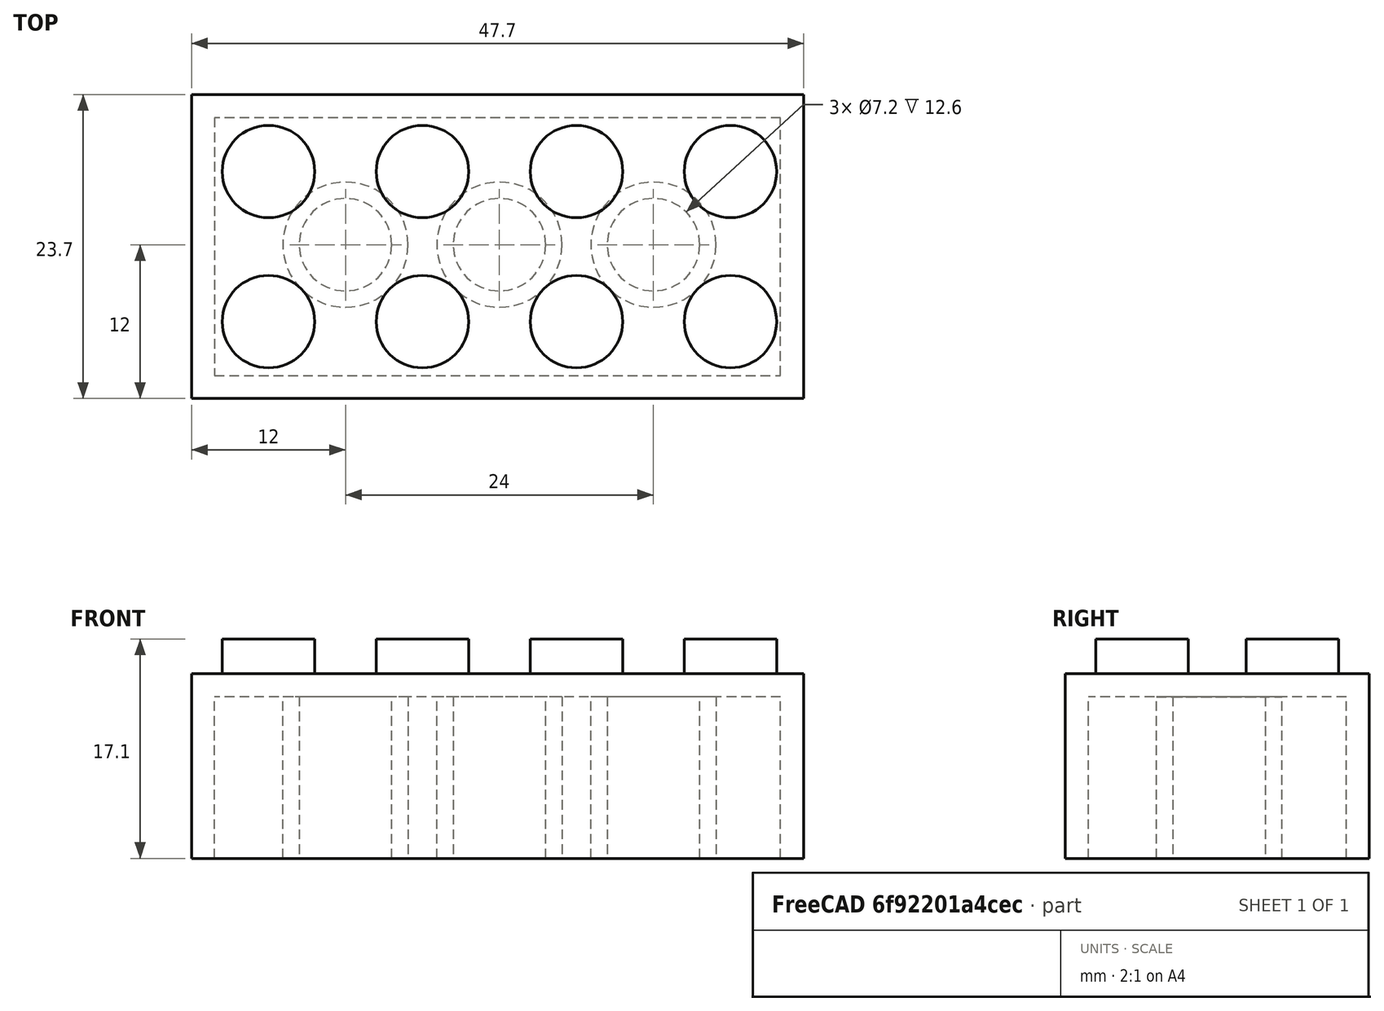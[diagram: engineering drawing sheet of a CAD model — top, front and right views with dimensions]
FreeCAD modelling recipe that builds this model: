
FCSTD DOCUMENT  (FreeCAD 0.19R17175 (Git))
Label: fem_lego
License: All rights reserved
LicenseURL: http://en.wikipedia.org/wiki/All_rights_reserved
objects: Sketcher::SketchObject×5, PartDesign::Pad×3, PartDesign::LinearPattern×3, PartDesign::Pocket×2, PartDesign::Body×1, Fem::FemMeshShapeNetgenObject×1, Fem::ConstraintFixed×1, Fem::ConstraintForce×1, App::MaterialObjectPython×1, Fem::FemSolverObjectPython×1, Fem::FemMeshObjectPython×1, Fem::FemResultObjectPython×1, Fem::FemAnalysis×1
note: 19 computed .brp shape members not serialized (recipe doc carries the construction recipe); baked Part::Feature solids carry a one-line shape summary decoded from their .brp

FEATURE [Sketcher::SketchObject] Sketch
  MapMode = 5
  Support = -> [XY_Plane]
  sketch-geometry (4):
    g0: LineSegment StartX=0 StartY=0 StartZ=0 EndX=47.7 EndY=0 EndZ=0
    g1: LineSegment StartX=47.7 StartY=0 StartZ=0 EndX=47.7 EndY=-23.7 EndZ=0
    g2: LineSegment StartX=47.7 StartY=-23.7 StartZ=0 EndX=0 EndY=-23.7 EndZ=0
    g3: LineSegment StartX=0 StartY=-23.7 StartZ=0 EndX=0 EndY=0 EndZ=0
  constraints (11):
    c: Coincident(g0,g1)
    c: Coincident(g1,g2)
    c: Coincident(g2,g3)
    c: Coincident(g3,g0)
    c: Horizontal(g0)
    c: Horizontal(g2)
    c: Vertical(g1)
    c: Vertical(g3)
    c: DistanceY(g3,g3) = 23.7
    c: DistanceX(g0,g0) = 47.7
    c: Coincident(g0,g-1)
FEATURE [PartDesign::Pad] Pad
  Length = 14.4
  Length2 = 100
  Profile = -> Sketch
  Type = 0
FEATURE [Sketcher::SketchObject] Sketch001
  ExternalGeometry = -> [Pad]
  MapMode = 5
  Placement = pos=(0,0,0) rot=(1,0,0;3.14159rad)
  Support = -> [Pad]
  sketch-geometry (4):
    g0: LineSegment StartX=1.8 StartY=21.9 StartZ=0 EndX=45.9 EndY=21.9 EndZ=0
    g1: LineSegment StartX=45.9 StartY=21.9 StartZ=0 EndX=45.9 EndY=1.8 EndZ=0
    g2: LineSegment StartX=45.9 StartY=1.8 StartZ=0 EndX=1.8 EndY=1.8 EndZ=0
    g3: LineSegment StartX=1.8 StartY=1.8 StartZ=0 EndX=1.8 EndY=21.9 EndZ=0
  constraints (12):
    c: Coincident(g0,g1)
    c: Coincident(g1,g2)
    c: Coincident(g2,g3)
    c: Coincident(g3,g0)
    c: Horizontal(g0)
    c: Horizontal(g2)
    c: Vertical(g1)
    c: Vertical(g3)
    c: DistanceX(g-4,g0) = 1.8
    c: DistanceY(g0,g-4) = 1.8
    c: DistanceX(g1,g-3) = 1.8
    c: DistanceY(g-3,g1) = 1.8
FEATURE [PartDesign::Pocket] Pocket
  BaseFeature = -> Pad
  Length = 12.6
  Length2 = 100
  Profile = -> Sketch001
  Type = 0
FEATURE [Sketcher::SketchObject] Sketch002
  ExternalGeometry = -> [Pocket]
  MapMode = 5
  Placement = pos=(0,0,14.4) rot=(0,0,1;0rad)
  Support = -> [Pocket]
  sketch-geometry (2):
    g0: Circle CenterX=6 CenterY=-6 CenterZ=0 NormalX=0 NormalY=0 NormalZ=1 AngleXU=0 Radius=3.6
    g1: Circle CenterX=6 CenterY=-17.7 CenterZ=0 NormalX=0 NormalY=0 NormalZ=1 AngleXU=0 Radius=3.6
  constraints (6):
    c: Radius(g0) = 3.6
    c: Radius(g1) = 3.6
    c: DistanceX(g-1,g0) = 6
    c: DistanceY(g0,g-1) = 6
    c: DistanceX(g-3,g1) = 6
    c: DistanceY(g-3,g1) = 6
FEATURE [PartDesign::Pad] Pad001
  BaseFeature = -> Pocket
  Length = 2.7
  Length2 = 100
  Profile = -> Sketch002
  Type = 0
FEATURE [PartDesign::LinearPattern] LinearPattern
  BaseFeature = -> Pad001
  Direction = -> Sketch002 [H_Axis]
  Length = 36
  Occurrences = 4
  Originals = -> [Pad001]
FEATURE [Sketcher::SketchObject] Sketch003
  ExternalGeometry = -> [LinearPattern]
  MapMode = 5
  Placement = pos=(0,0,12.6) rot=(1,0,0;3.14159rad)
  Support = -> [LinearPattern]
  sketch-geometry (1):
    g0: Circle CenterX=12 CenterY=11.7 CenterZ=0 NormalX=0 NormalY=0 NormalZ=1 AngleXU=0 Radius=4.8825
  constraints (3):
    c: Radius(g0) = 4.8825
    c: DistanceX(g-3,g0) = 10.2
    c: DistanceY(g0,g-3) = 10.2
FEATURE [PartDesign::Pad] Pad002
  BaseFeature = -> LinearPattern
  Length = 12.6
  Length2 = 100
  Profile = -> Sketch003
  Type = 0
FEATURE [PartDesign::LinearPattern] LinearPattern001
  BaseFeature = -> Pad002
  Direction = -> Sketch003 [H_Axis]
  Length = 24
  Occurrences = 3
  Originals = -> [Pad002]
FEATURE [Sketcher::SketchObject] Sketch004
  ExternalGeometry = -> [LinearPattern001]
  MapMode = 5
  Placement = pos=(0,0,1.8e-15) rot=(1,0,0;3.14159rad)
  Support = -> [LinearPattern001]
  sketch-geometry (1):
    g0: Circle CenterX=12 CenterY=11.7 CenterZ=0 NormalX=0 NormalY=0 NormalZ=1 AngleXU=0 Radius=3.6
  constraints (2):
    c: Coincident(g0,g-3)
    c: Radius(g0) = 3.6
FEATURE [PartDesign::Pocket] Pocket001
  BaseFeature = -> LinearPattern001
  Length = 12.6
  Length2 = 100
  Profile = -> Sketch004
  Type = 0
FEATURE [PartDesign::LinearPattern] LinearPattern002
  BaseFeature = -> Pocket001
  Direction = -> Sketch004 [H_Axis]
  Length = 24
  Occurrences = 3
  Originals = -> [Pocket001]
FEATURE [PartDesign::Body] Body
  Group = -> [Sketch,Pad,Sketch001,Pocket,Sketch002,Pad001,LinearPattern,Sketch003,Pad002,LinearPattern001,Sketch004,Pocket001,LinearPattern002]
  Origin = -> Origin
  Tip = -> LinearPattern002
FEATURE [Fem::FemMeshShapeNetgenObject] FEMMeshNetgen
  Fineness = 2
  GrowthRate = 0.3
  MaxSize = 1000
  NbSegsPerEdge = 1
  NbSegsPerRadius = 2
  Optimize = true
  SecondOrder = true
  Shape = -> Body
FEATURE [Fem::ConstraintFixed] FemConstraintFixed
  NormalDirection = (-1,0,0)
  Normals = (9) [(-1,0,0),(-1,0,0),(-1,0,0),(-1,0,0),(-1,0,0),(-1,0,0),(-1,0,0),(-1,0,0),(-1,0,0)]
  Points = (9) [(0,-23.7,14.4),(0,-11.85,14.4),(0,0,14.4),(0,-23.7,7.2),(0,-11.85,7.2),(0,0,7.2),(0,-23.7,0),(0,-11.85,0),(0,0,0)]
  References = -> [LinearPattern002]
FEATURE [Fem::ConstraintForce] FemConstraintForce
  DirectionVector = (1,0,0)
  Force = 9000000
  NormalDirection = (1,0,0)
  Points = (9) [(47.7,0,14.4),(47.7,-11.85,14.4),(47.7,-23.7,14.4),(47.7,0,7.2),(47.7,-11.85,7.2),(47.7,-23.7,7.2),(47.7,0,0),(47.7,-11.85,0),(47.7,-23.7,0)]
  References = -> [LinearPattern002]
FEATURE [App::MaterialObjectPython] SolidMaterial  # material (typed FeaturePython)
  Category = 0
  Material = AuthorAndLicense=CalculiX-Steel,CardName=CalculiX-Steel,Density=7900 kg/m^3,Description=Standard steel material for CalculiX sample calculations,+7 more (map truncated)
FEATURE [Fem::FemSolverObjectPython] CalculiXccxTools  # FEM object (typed FeaturePython)
  AnalysisType = 0
  BeamShellResultOutput3D = false
  EigenmodeHighLimit = 1000000
  EigenmodeLowLimit = 0
  EigenmodesCount = 10
  GeometricalNonlinearity = 0
  IterationsControlParameterCutb = 0.25,0.5,0.75,0.85,,,1.5,
  IterationsControlParameterIter = 4,8,9,200,10,400,,200,,
  IterationsControlParameterTimeUse = false
  IterationsThermoMechMaximum = 200
  IterationsUserDefinedIncrementations = false
  IterationsUserDefinedTimeStepLength = false
  MaterialNonlinearity = 0
  MatrixSolverType = 0
  SplitInputWriter = false
  ThermoMechSteadyState = true
  TimeEnd = 1
  TimeInitialStep = 1
FEATURE [Fem::FemMeshObjectPython] Result_mesh  # FEM object (typed FeaturePython)
FEATURE [Fem::FemResultObjectPython] CalculiX_static_results  # FEM object (typed FeaturePython)
  DisplacementLengths = [28.4265,10.9117,45.7766,37.8963,18.8004,52.0495,39.2825,19.4572,53.3285,30.3354,12.2282,47.5529,66.8887,66.6993,37.4693,37.5044,17.1379,17.0912,3.22552,3.24594,72.37,72.3182,0.455421,0.445806,68.2837,68.258,38.0674,38.1103,17.6461,17.6119,+15129 more]
  DisplacementVectors = (15159) [(7.98861,-0.0382985,27.2809),(4.54064,-0.0181082,9.92208),(13.3608,-0.0256765,43.7834),(26.3049,-0.1859,27.2791),(16.0371,-0.134093,9.81071),+15154 more]
  Eigenmode = 0
  EigenmodeFrequency = 0
  MaxShear = [35883,28616.5,110972,1467.28,341.145,8719.95,534.307,1626.88,3521.59,35231.6,26596.6,99043.4,20993.6,14314.9,6094.94,6538.09,5295.15,5488.07,3480.28,3881.23,86180.6,83484.9,30359.4,29876.7,88140.7,183186,59519,59311.8,25453.8,26944.6,+15129 more]
  Mesh = -> Result_mesh
  NodeNumbers = [1,2,3,4,5,6,7,8,9,10,11,12,13,14,15,16,17,18,19,20,21,22,23,24,25,26,27,28,29,30,31,32,33,34,35,36,37,38,39,40,41,42,43,44,45,46,47,48,49,50,51,52,53,54,55,56,57,58,59,60,61,62,63,64,65,66,67,68,69,+15090 more]
  NodeStrainXX = [0.279929,0.243832,0.79047,-0.0037722,-3.29326e-05,-0.0204668,-0.00114947,-0.00458861,0.0103888,0.295332,0.275277,0.910516,-0.00535909,-0.0143347,-0.0215639,-0.0174807,-0.0217403,-0.0175679,-0.00807231,-0.00395808,0.274491,0.236876,0.257209,+15136 more]
  NodeStrainXY = [0.00600801,0.000272015,-0.0257815,-0.00022686,3.13159e-05,0.00352629,0.00057828,0.000174495,-8.91894e-05,0.000894787,-0.00055564,0.0068005,0.0248579,-0.0108751,0.00298216,0.00255899,-0.00206303,0.00110538,0.00188108,-0.00436349,0.140462,+15138 more]
  NodeStrainXZ = [-0.0645909,-0.0600872,-0.122988,-0.000106265,0.000363592,-0.0019615,-0.000130782,-5.01476e-05,7.35259e-05,0.0597871,0.0685975,0.0467278,-0.0332973,-0.037656,0.00620316,0.000495662,0.00117294,0.000699152,-0.00220768,-0.00320543,-0.129079,+15138 more]
  NodeStrainYY = [-0.15273,-0.0715412,-0.133961,0.014147,-0.00259966,0.0819441,0.00471246,0.0153213,-0.0331932,-0.129453,-0.038416,0.105206,0.173042,0.107888,0.0498068,0.0621764,0.0433789,0.0491646,0.0279815,0.0338794,-0.0630916,-0.0441522,-0.0698721,+15136 more]
  NodeStrainYZ = [-0.00137281,0.00205578,-0.0118947,-0.00121229,-0.000531947,0.00137185,0.000182438,0.000119575,-0.000719144,0.00431451,0.00121926,0.00279703,-0.0287185,0.0214905,-0.000427537,-0.00533391,0.00293694,-0.00402519,-0.00613062,0.00510437,+15139 more]
  NodeStrainZZ = [-0.0734525,-0.089303,-0.56014,-0.0037615,0.00140247,-0.0251025,-0.00180322,-0.00480664,0.00946767,-0.0112268,-0.0152249,-0.312097,-0.0626147,-0.0343334,-0.0154714,-0.0174107,-0.0116391,-0.0176618,-0.012546,-0.0116271,-0.0568265,-0.0807173,+15137 more]
  NodeStressXX = [51730.9,49442.6,139367,191.867,-154.354,1100.76,27.5178,-23.2677,62.3942,66444.1,71319.8,232330,11863.7,4859.14,-1936.08,481.869,-2300.41,-1149.63,-411.906,1577.03,63068.1,51834.5,55983.3,57001.7,-164079,-341557,73236.2,78112.1,40402.5,+15130 more]
  NodeStressXY = [970.524,43.941,-4164.7,-36.6466,5.05871,569.631,93.4144,28.1876,-14.4075,144.542,-89.7573,1098.54,4015.51,-1756.74,481.733,413.376,-333.259,178.561,303.867,-704.872,22689.9,-21923.6,2298.68,-1816.07,61553.5,-106305,-41625.8,42292,330.668,+15130 more]
  NodeStressXZ = [-10433.9,-9706.39,-19867.3,-17.1659,58.7341,-316.858,-21.1263,-8.10077,11.8773,9657.91,11081.1,7548.33,-5378.79,-6082.9,1002.05,80.0685,189.475,112.94,-356.625,-517.801,-20851.3,-20749.7,-3361.08,-2375.71,40742.2,88505.3,-12347,-11545.3,+15131 more]
  NodeStressYY = [-18160.1,-1502.33,-9964.51,3086.5,-568.979,17644.1,974.445,3192.95,-6977.77,-2175.01,20646.4,102242,40682.3,24602.8,9593.03,13349.6,8218.85,9630.24,5412.17,7689.23,8535.44,6437.71,3147.16,4253.88,-68491.9,-111105,-376.738,1636.11,8008.86,+15130 more]
  NodeStressYZ = [-221.762,332.087,-1921.45,-195.831,-85.9299,221.607,29.4708,19.3159,-116.169,696.959,196.958,451.827,-4639.14,3471.54,-69.0636,-861.632,474.429,-650.224,-990.331,824.552,-75183.1,73348.6,7474.88,-7231.66,3522.48,-8876.96,17547.6,-12856.3,+15131 more]
  NodeStressZZ = [-5353.77,-4371.54,-78808.8,193.595,77.5178,351.927,-78.0867,-58.4891,-86.4013,16923.1,24392.6,34831.4,2614.72,1628.59,-951.92,493.173,-668.674,-1164.79,-1134.58,338.18,9547.5,531.049,3417.66,5341.4,-77473.5,-108928,10973.7,11713.3,-10482.3,+15130 more]
  PrincipalMax = [53592,51139.8,141266,3100.13,101.706,17666.3,984.273,3193.31,63.4161,68262,73804.9,232628,41965.4,25474.4,9613.19,13419.9,8253.98,9671.98,5579.52,7872.12,106202,97045.6,56260.9,57153.1,-27839.9,-38299.6,96051.8,99728.5,40415,43522.8,+15129 more]
  PrincipalMed = [-7200.87,-1477.93,-9994.88,206.269,-166.937,1204.17,23.943,-21.6634,-85.4368,15131.2,21942.2,102235,13217.2,8771.4,-331.486,561.017,-667.887,-1052.01,-332.797,1622.65,41108.5,31681.7,10745.1,12044.1,-78083.3,-118619,10767.5,10628.2,8006.82,+15130 more]
  PrincipalMin = [-18174.1,-6093.14,-80677.3,165.565,-580.584,226.359,-84.34,-60.4543,-6979.76,-2201.08,20611.7,34540.8,-21.8309,-3155.3,-2576.68,343.724,-2336.32,-1304.15,-1381.04,109.669,-66159.4,-69924.1,-4457.94,-2600.2,-204121,-404671,-22986.1,-18895.2,+15131 more]
  ResultType = Fem::FemResultMechanical
  Stats = [-1.50025,16.408,282.988,-83.7111,0.065326,83.5169,-0.552481,25.414,100.445,0,33.8857,300.195,22.6659,84139.5,1056800,-93547.1,65314.5,1105060,-265120,4436.43,383002,-1042050,-25189.6,315360,13.0052,45252,544304,0,0,0,0,0,0,0,0,0,0,0,0]
  StressValues = [66957.3,55070.6,196386,2914.42,595.312,16972.1,1018.8,3234.54,6969.94,63593.8,52540.5,174389,37179.7,24908.8,11236.8,12968.9,9862.5,10852.3,6500.14,7127.44,150751,145731,54724.8,53943.2,157298,333546,106261,106963,44632.5,47278.6,38673,+15128 more]
  Time = 0
FEATURE [Fem::FemAnalysis] Analysis
  Group = -> [FEMMeshNetgen,FemConstraintFixed,FemConstraintForce,SolidMaterial,CalculiXccxTools,CalculiX_static_results]
